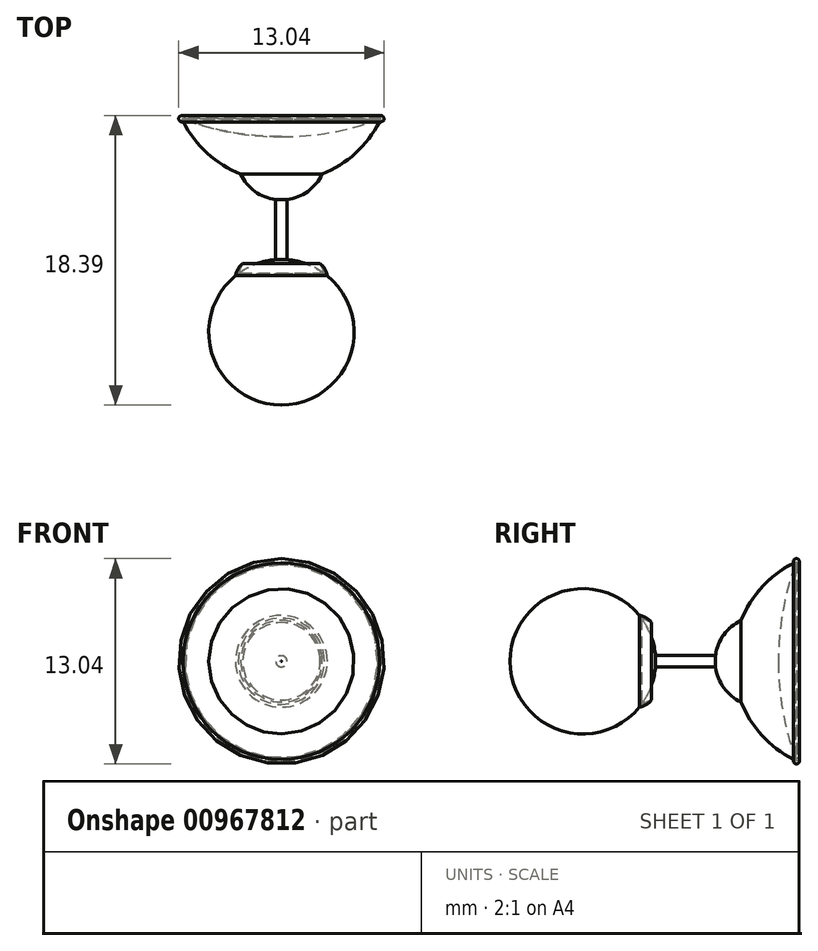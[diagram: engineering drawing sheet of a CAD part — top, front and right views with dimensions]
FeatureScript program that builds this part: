
annotation { "Feature Type Name" : "Feature", "Feature Type Description" : "" }
export const myFeature = defineFeature(function(context is Context, id is Id, definition is map)
    precondition{}
    {
        {
            var Q0;
            Q0=qCreatedBy(makeId("Top.planeOp"),FACE);
            var sketch = newSketch(context, id + "F0", { "sketchPlane" : qUnion([Q0])});
            skArc(sketch, "E0", {"start": v(0, 0) * mm, "mid": v(3.1, -0.86) * mm, "end": v(6.32, -1.14) * mm});
            skArc(sketch, "E1", {"start": v(0, 0) * mm, "mid": v(2.58, -2.92) * mm, "end": v(6.32, -4) * mm});
            skLineSegment(sketch, "E2", {"start": v(6.32, -1.14) * mm, "end": v(6.32, -4) * mm});
            skCircle(sketch, "E3", {"center": v(0, 0) * mm, "radius": 0.2 * mm});
            skPoint(sketch, "E4.end.orphan", {"position": v(3.73, -3.51) * mm});
            skPoint(sketch, "E5.end.orphan", {"position": v(5.96, -5.13) * mm});
            skPoint(sketch, "E6.end.orphan", {"position": v(6.66, -5.13) * mm});
            skPoint(sketch, "E7.end.orphan", {"position": v(8.91, -3.51) * mm});
            skArc(sketch, "E8", {"start": v(3.73, -3.51) * mm, "mid": v(4.79, -4.71) * mm, "end": v(6.32, -5.16) * mm});
            skLineSegment(sketch, "E9", {"start": v(5.96, -5.13) * mm, "end": v(5.96, -8.94) * mm});
            skLineSegment(sketch, "E10", {"start": v(5.96, -8.94) * mm, "end": v(6.32, -8.94) * mm});
            skPoint(sketch, "E11.orphan", {"position": v(12.64, 0) * mm});
            skLineSegment(sketch, "E12", {"start": v(6.32, -4) * mm, "end": v(6.32, -18.05) * mm});
            skArc(sketch, "E13", {"start": v(6.32, -8.94) * mm, "mid": v(4.78, -9.2) * mm, "end": v(3.4, -9.97) * mm});
            skLineSegment(sketch, "E14", {"start": v(3.4, -9.97) * mm, "end": v(6.32, -9.97) * mm});
            skArc(sketch, "E15", {"start": v(3.86, -9.2) * mm, "mid": v(3.56, -9.54) * mm, "end": v(3.4, -9.97) * mm});
            skPoint(sketch, "E15.startSnap0", {"position": v(4.78, -9.2) * mm});
            skLineSegment(sketch, "E16", {"start": v(3.86, -9.2) * mm, "end": v(3.58, -9.83) * mm});
            skSolve(sketch);
        }
        {
            var Q0;
            {var subQ3=sQuery(id+"F0.wireOp",EDGE,"E2");Q0=makeQuery(id+"F0.imprint","IMPRINT",FACE,{"disambiguationData":[TD([[makeQuery(id+"F0.imprint","IMPRINT",EDGE,{"derivedFrom":subQ3}),1.0]])]});}
            var Q1;
            {var subQ0=sQuery(id+"F0.wireOp",EDGE,"E1");var subQ1=sQuery(id+"F0.wireOp",EDGE,"E0");var subQ2=makeQuery(id+"F0.imprint","INTERSECT",VERTEX,{"disambiguationData":[OD(0.0)],"derivedFrom":[subQ1,subQ0]});Q1=makeQuery(id+"F0.imprint","IMPRINT",FACE,{"disambiguationData":[TD([[makeQuery(id+"F0.imprint","IMPRINT",EDGE,{"disambiguationData":[TD([[subQ2,-1.0]])],"derivedFrom":subQ1}),1.0]])]});}
            var Q2;
            {var subQ0=sQuery(id+"F0.wireOp",EDGE,"E2");Q2=makeQuery(id+"F0.imprint","IMPRINT",FACE,{"disambiguationData":[TD([[makeQuery(id+"F0.imprint","IMPRINT",EDGE,{"derivedFrom":subQ0}),-1.0]])]});}
            var Q3;
            {var subQ1=sQuery(id+"F0.wireOp",EDGE,"E1");var subQ3=sQuery(id+"F0.wireOp",EDGE,"E8");var subQ4=makeQuery(id+"F0.imprint","INTERSECT",VERTEX,{"derivedFrom":[subQ1,subQ3]});Q3=makeQuery(id+"F0.imprint","IMPRINT",FACE,{"disambiguationData":[TD([[makeQuery(id+"F0.imprint","IMPRINT",EDGE,{"disambiguationData":[TD([[subQ4,-1.0]])],"derivedFrom":subQ3}),1.0]])]});}
            var Q4;
            {var subQ5=sQuery(id+"F0.wireOp",EDGE,"E10");Q4=makeQuery(id+"F0.imprint","IMPRINT",FACE,{"disambiguationData":[TD([[makeQuery(id+"F0.imprint","IMPRINT",EDGE,{"derivedFrom":subQ5}),1.0]])]});}
            var Q5;
            {var subQ3=sQuery(id+"F0.wireOp",EDGE,"E14");Q5=makeQuery(id+"F0.imprint","IMPRINT",FACE,{"disambiguationData":[TD([[makeQuery(id+"F0.imprint","IMPRINT",EDGE,{"derivedFrom":subQ3}),1.0]])]});}
            var Q6;
            {var subQ0=sQuery(id+"F0.wireOp",EDGE,"E15");Q6=makeQuery(id+"F0.imprint","IMPRINT",FACE,{"disambiguationData":[TD([[makeQuery(id+"F0.imprint","IMPRINT",EDGE,{"derivedFrom":subQ0}),1.0]])]});}
            var Q7;
            Q7=sQuery(id+"F0.wireOp",EDGE,"E2");
            revolve(context, id + "F1", {"surfaceOperationType" : NewSurfaceOperationType.NEW, "entities" : qUnion([Q0, Q1, Q2, Q3, Q4, Q5, Q6]), "axis" : qUnion([Q7]), "revolveType" : RevolveType.SYMMETRIC, "angle" : 360 * degree});
        }
    });
